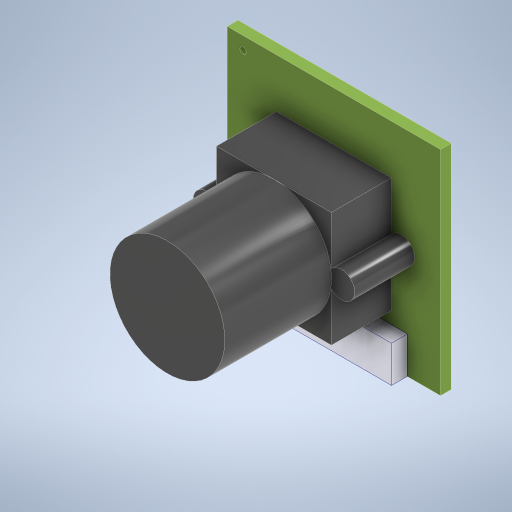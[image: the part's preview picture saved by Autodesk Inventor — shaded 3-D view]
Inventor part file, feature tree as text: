
AUTODESK INVENTOR PART (.ipt)
format: ipt  version: 2023 (Build 270158000, 158)  size: 290,816 bytes
history: native  units: mm
features: extrude x5, other x3, sketch x1
ambient origin geometry x8: Origin, YZ Plane, XZ Plane, XY Plane, X Axis, Y Axis, Z Axis, Center Point
bodies: Body1 (feature_tree), Body2 (feature_tree), Body3 (feature_tree)
feature tree (9):
  other  "Sólido1"
  sketch  "Boceto1"  dims[d0=32.0mm d1=22.0mm d2=5.5mm d3=17.25mm d4=4.0mm d6=1.5mm d7=1.5mm d8=9.0mm d9=0.0mm d10=1.61mm d11=0.0mm d12=2.35mm d13=0.0mm d14=25.0mm d15=0.0mm d16=13.625mm d17=2.0mm d18=1.0mm d19=25.0mm d20=0.0mm]
  extrude  "Extrusión1"  Depth=22.0mm
  extrude  "Extrusión2"  Depth=5.5mm
  extrude  "Extrusión3"  Depth=17.25mm
  extrude  "Extrusión4"  Depth=25.0mm
  extrude  "Extrusión5"  Depth=25.0mm
  other  "Sólido2"
  other  "Sólido3"
